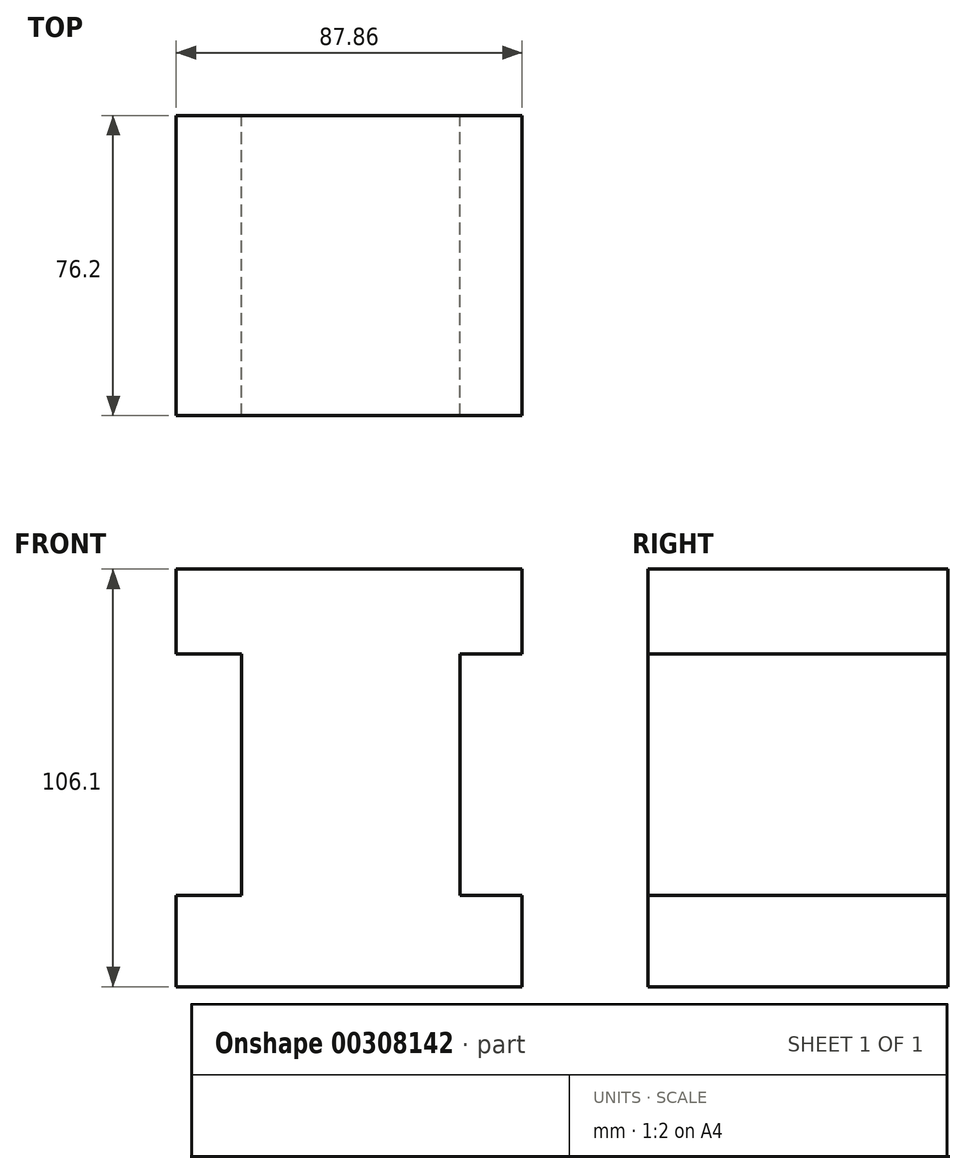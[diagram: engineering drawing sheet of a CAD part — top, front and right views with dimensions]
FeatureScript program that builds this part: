
annotation { "Feature Type Name" : "Feature", "Feature Type Description" : "" }
export const myFeature = defineFeature(function(context is Context, id is Id, definition is map)
    precondition{}
    {
        {
            var Q0;
            Q0=qCreatedBy(makeId("Front.planeOp"),FACE);
            var sketch = newSketch(context, id + "F0", { "sketchPlane" : qUnion([Q0])});
            skLineSegment(sketch, "E0", {"start": v(-42.22, -33.8) * mm, "end": v(45.64, -33.8) * mm});
            skLineSegment(sketch, "E1", {"start": v(45.64, -33.8) * mm, "end": v(45.64, -10.58) * mm});
            skLineSegment(sketch, "E2", {"start": v(45.64, -10.58) * mm, "end": v(29.92, -10.58) * mm});
            skLineSegment(sketch, "E3", {"start": v(29.92, -10.58) * mm, "end": v(29.92, 50.78) * mm});
            skLineSegment(sketch, "E4", {"start": v(29.92, 50.78) * mm, "end": v(45.64, 50.78) * mm});
            skLineSegment(sketch, "E5", {"start": v(45.64, 50.78) * mm, "end": v(45.64, 72.3) * mm});
            skLineSegment(sketch, "E6", {"start": v(45.64, 72.3) * mm, "end": v(-42.22, 72.3) * mm});
            skLineSegment(sketch, "E7", {"start": v(-42.22, 72.3) * mm, "end": v(-42.22, 50.78) * mm});
            skLineSegment(sketch, "E8", {"start": v(-42.22, 50.78) * mm, "end": v(-25.65, 50.78) * mm});
            skLineSegment(sketch, "E9", {"start": v(-25.65, 50.78) * mm, "end": v(-25.65, -10.58) * mm});
            skLineSegment(sketch, "E10", {"start": v(-25.65, -10.58) * mm, "end": v(-42.22, -10.58) * mm});
            skLineSegment(sketch, "E11", {"start": v(-42.22, -10.58) * mm, "end": v(-42.22, -33.8) * mm});
            skSolve(sketch);
        }
        {
            var Q0;
            Q0=makeQuery(id+"F0.imprint","IMPRINT",FACE,{"disambiguationData":[TD([[makeQuery(id+"F0.imprint","IMPRINT",EDGE,{"derivedFrom":sQuery(id+"F0.wireOp",EDGE,"E0")}),1.0]])]});
            extrude(context, id + "F1", {"entities" : qUnion([Q0]), "depth" : 76.2 * mm});
        }
    });
